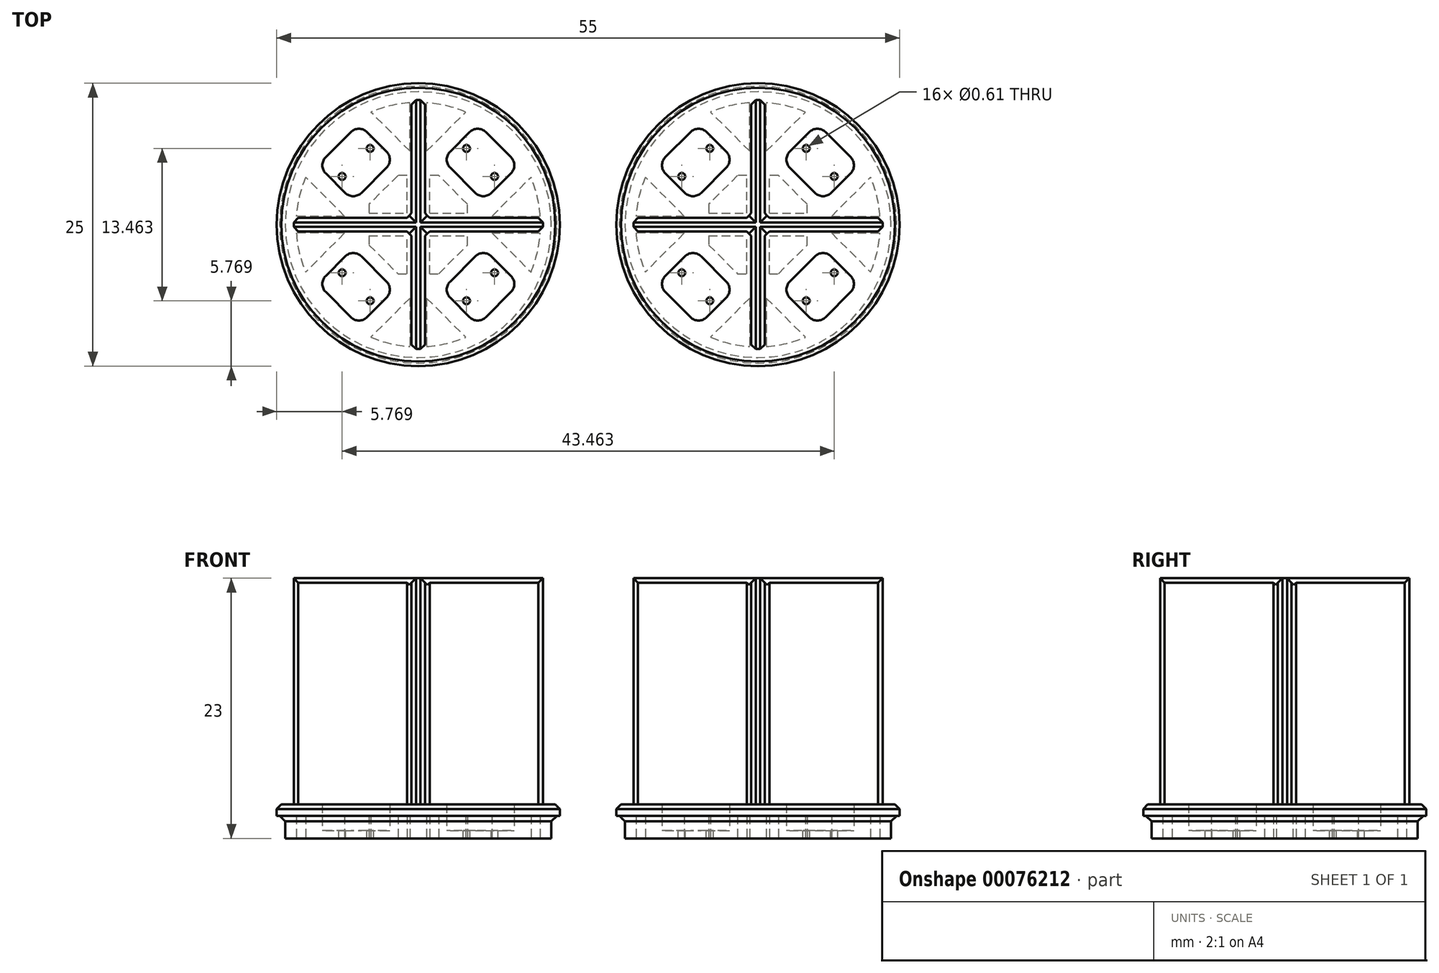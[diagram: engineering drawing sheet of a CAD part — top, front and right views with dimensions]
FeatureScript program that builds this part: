
annotation { "Feature Type Name" : "Feature", "Feature Type Description" : "" }
export const myFeature = defineFeature(function(context is Context, id is Id, definition is map)
    precondition{}
    {
        {
            var Q0;
            Q0=qCreatedBy(makeId("Top.planeOp"),FACE);
            var sketch = newSketch(context, id + "F0", { "sketchPlane" : qUnion([Q0])});
            skCircle(sketch, "E0", {"center": v(0, 0) * mm, "radius": 12.5 * mm});
            skSolve(sketch);
        }
        {
            var Q0;
            Q0=makeQuery(id+"F0.imprint","IMPRINT",FACE,{"disambiguationData":[TD([[makeQuery(id+"F0.imprint","IMPRINT",EDGE,{"derivedFrom":sQuery(id+"F0.wireOp",EDGE,"E0")}),1.0]])]});
            extrude(context, id + "F1", {"entities" : qUnion([Q0]), "depth" : 3 * mm});
        }
        {
            var Q0;
            Q0=makeQuery(id+"F1.opExtrude","CAP_FACE",FACE,{"disambiguationData":[OSD([sQuery(id+"F0.wireOp",EDGE,"E0")])],"isStart":false});
            var sketch = newSketch(context, id + "F2", { "sketchPlane" : qUnion([Q0])});
            skLineSegment(sketch, "E1", {"start": v(0, 0) * mm, "end": v(12.5, 0) * mm});
            skLineSegment(sketch, "E2", {"start": v(0, 0) * mm, "end": v(0, 12.5) * mm});
            skLineSegment(sketch, "E3.0", {"start": v(5.25, 8.89) * mm, "end": v(8.89, 5.25) * mm});
            skLineSegment(sketch, "E3.1", {"start": v(8.89, 5.25) * mm, "end": v(5.74, 2.1) * mm});
            skLineSegment(sketch, "E3.2", {"start": v(5.74, 2.1) * mm, "end": v(2.1, 5.74) * mm});
            skLineSegment(sketch, "E3.3", {"start": v(2.1, 5.74) * mm, "end": v(5.25, 8.89) * mm});
            skPoint(sketch, "E4.center", {"position": v(0, 0) * mm});
            skLineSegment(sketch, "E5.1.0", {"start": v(5.74, -2.1) * mm, "end": v(8.89, -5.25) * mm});
            skLineSegment(sketch, "E5.1.1", {"start": v(8.89, -5.25) * mm, "end": v(5.25, -8.89) * mm});
            skLineSegment(sketch, "E5.1.2", {"start": v(2.1, -5.74) * mm, "end": v(5.74, -2.1) * mm});
            skLineSegment(sketch, "E5.1.3", {"start": v(5.25, -8.89) * mm, "end": v(2.1, -5.74) * mm});
            skLineSegment(sketch, "E5.2.0", {"start": v(-2.1, -5.74) * mm, "end": v(-5.25, -8.89) * mm});
            skLineSegment(sketch, "E5.2.1", {"start": v(-5.25, -8.89) * mm, "end": v(-8.89, -5.25) * mm});
            skLineSegment(sketch, "E5.2.2", {"start": v(-5.74, -2.1) * mm, "end": v(-2.1, -5.74) * mm});
            skLineSegment(sketch, "E5.2.3", {"start": v(-8.89, -5.25) * mm, "end": v(-5.74, -2.1) * mm});
            skLineSegment(sketch, "E5.3.0", {"start": v(-5.74, 2.1) * mm, "end": v(-8.89, 5.25) * mm});
            skLineSegment(sketch, "E5.3.1", {"start": v(-8.89, 5.25) * mm, "end": v(-5.25, 8.89) * mm});
            skLineSegment(sketch, "E5.3.2", {"start": v(-2.1, 5.74) * mm, "end": v(-5.74, 2.1) * mm});
            skLineSegment(sketch, "E5.3.3", {"start": v(-5.25, 8.89) * mm, "end": v(-2.1, 5.74) * mm});
            skLineSegment(sketch, "E5.anchor1", {"start": v(0, 0) * mm, "end": v(2.1, 5.74) * mm, "construction": true});
            skLineSegment(sketch, "E5.anchor2", {"start": v(0, 0) * mm, "end": v(-5.74, 2.1) * mm, "construction": true});
            skSolve(sketch);
        }
        {
            var Q0;
            Q0=makeQuery(id+"F2.imprint","IMPRINT",FACE,{"disambiguationData":[TD([[makeQuery(id+"F2.imprint","IMPRINT",EDGE,{"derivedFrom":sQuery(id+"F2.wireOp",EDGE,"E5.3.0")}),-1.0]])]});
            var Q1;
            Q1=makeQuery(id+"F2.imprint","IMPRINT",FACE,{"disambiguationData":[TD([[makeQuery(id+"F2.imprint","IMPRINT",EDGE,{"derivedFrom":sQuery(id+"F2.wireOp",EDGE,"E3.0")}),-1.0]])]});
            var Q2;
            Q2=makeQuery(id+"F2.imprint","IMPRINT",FACE,{"disambiguationData":[TD([[makeQuery(id+"F2.imprint","IMPRINT",EDGE,{"derivedFrom":sQuery(id+"F2.wireOp",EDGE,"E5.1.0")}),-1.0]])]});
            var Q3;
            Q3=makeQuery(id+"F2.imprint","IMPRINT",FACE,{"disambiguationData":[TD([[makeQuery(id+"F2.imprint","IMPRINT",EDGE,{"derivedFrom":sQuery(id+"F2.wireOp",EDGE,"E5.2.0")}),-1.0]])]});
            extrude(context, id + "F3", {"entities" : qUnion([Q0, Q1, Q2, Q3]), "operationType" : NewBodyOperationType.REMOVE, "oppositeDirection" : true, "depth" : 2.3 * mm});
        }
        {
            var Q0;
            Q0=makeQuery(id+"F3.boolean.opBoolean","COPY",FACE,{"derivedFrom":makeQuery(id+"F3.opExtrude","CAP_FACE",FACE,{"disambiguationData":[OSD([sQuery(id+"F2.wireOp",EDGE,"E3.0"),sQuery(id+"F2.wireOp",EDGE,"E3.1"),sQuery(id+"F2.wireOp",EDGE,"E3.2"),sQuery(id+"F2.wireOp",EDGE,"E3.3")])],"isStart":false})});
            var sketch = newSketch(context, id + "F4", { "sketchPlane" : qUnion([Q0])});
            skCircle(sketch, "E6", {"center": v(4.26, 6.73) * mm, "radius": 0.3 * mm});
            skCircle(sketch, "E7", {"center": v(6.73, 4.26) * mm, "radius": 0.3 * mm});
            skPoint(sketch, "E8.orphan", {"position": v(5.83, 8.3) * mm});
            skPoint(sketch, "E9.orphan", {"position": v(2.68, 5.16) * mm});
            skPoint(sketch, "E10.orphan", {"position": v(3.67, 7.31) * mm});
            skPoint(sketch, "E11.orphan", {"position": v(7.07, 7.07) * mm});
            skPoint(sketch, "E12.start.orphan", {"position": v(3.92, 3.92) * mm});
            skPoint(sketch, "E13.orphan", {"position": v(5.16, 2.68) * mm});
            skPoint(sketch, "E14.orphan", {"position": v(8.3, 5.83) * mm});
            skPoint(sketch, "E15.orphan", {"position": v(7.31, 3.67) * mm});
            skCircle(sketch, "E16.1.0", {"center": v(6.73, -4.26) * mm, "radius": 0.3 * mm});
            skCircle(sketch, "E16.1.1", {"center": v(4.26, -6.73) * mm, "radius": 0.3 * mm});
            skCircle(sketch, "E16.2.0", {"center": v(-4.26, -6.73) * mm, "radius": 0.3 * mm});
            skCircle(sketch, "E16.2.1", {"center": v(-6.73, -4.26) * mm, "radius": 0.3 * mm});
            skCircle(sketch, "E16.3.0", {"center": v(-6.73, 4.26) * mm, "radius": 0.3 * mm});
            skCircle(sketch, "E16.3.1", {"center": v(-4.26, 6.73) * mm, "radius": 0.3 * mm});
            skPoint(sketch, "E16.center", {"position": v(0, 0) * mm});
            skLineSegment(sketch, "E16.anchor1", {"start": v(0, 0) * mm, "end": v(4.26, 6.73) * mm, "construction": true});
            skLineSegment(sketch, "E16.anchor2", {"start": v(0, 0) * mm, "end": v(-6.73, 4.26) * mm, "construction": true});
            skSolve(sketch);
        }
        {
            var Q0;
            Q0=makeQuery(id+"F4.imprint","IMPRINT",FACE,{"disambiguationData":[TD([[makeQuery(id+"F4.imprint","IMPRINT",EDGE,{"derivedFrom":sQuery(id+"F4.wireOp",EDGE,"E16.3.1")}),1.0]])]});
            var Q1;
            Q1=makeQuery(id+"F4.imprint","IMPRINT",FACE,{"disambiguationData":[TD([[makeQuery(id+"F4.imprint","IMPRINT",EDGE,{"derivedFrom":sQuery(id+"F4.wireOp",EDGE,"E16.3.0")}),1.0]])]});
            var Q2;
            Q2=makeQuery(id+"F4.imprint","IMPRINT",FACE,{"disambiguationData":[TD([[makeQuery(id+"F4.imprint","IMPRINT",EDGE,{"derivedFrom":sQuery(id+"F4.wireOp",EDGE,"E6")}),1.0]])]});
            var Q3;
            Q3=makeQuery(id+"F4.imprint","IMPRINT",FACE,{"disambiguationData":[TD([[makeQuery(id+"F4.imprint","IMPRINT",EDGE,{"derivedFrom":sQuery(id+"F4.wireOp",EDGE,"E7")}),1.0]])]});
            var Q4;
            Q4=makeQuery(id+"F4.imprint","IMPRINT",FACE,{"disambiguationData":[TD([[makeQuery(id+"F4.imprint","IMPRINT",EDGE,{"derivedFrom":sQuery(id+"F4.wireOp",EDGE,"E16.1.0")}),1.0]])]});
            var Q5;
            Q5=makeQuery(id+"F4.imprint","IMPRINT",FACE,{"disambiguationData":[TD([[makeQuery(id+"F4.imprint","IMPRINT",EDGE,{"derivedFrom":sQuery(id+"F4.wireOp",EDGE,"E16.1.1")}),1.0]])]});
            var Q6;
            Q6=makeQuery(id+"F4.imprint","IMPRINT",FACE,{"disambiguationData":[TD([[makeQuery(id+"F4.imprint","IMPRINT",EDGE,{"derivedFrom":sQuery(id+"F4.wireOp",EDGE,"E16.2.0")}),1.0]])]});
            var Q7;
            Q7=makeQuery(id+"F4.imprint","IMPRINT",FACE,{"disambiguationData":[TD([[makeQuery(id+"F4.imprint","IMPRINT",EDGE,{"derivedFrom":sQuery(id+"F4.wireOp",EDGE,"E16.2.1")}),1.0]])]});
            extrude(context, id + "F5", {"entities" : qUnion([Q0, Q1, Q2, Q3, Q4, Q5, Q6, Q7]), "operationType" : NewBodyOperationType.REMOVE, "endBound" : BoundingType.UP_TO_NEXT, "oppositeDirection" : true, "depth" : 25 * mm});
        }
        {
            var Q0;
            Q0=makeQuery(id+"F3.boolean.opBoolean","COPY",EDGE,{"derivedFrom":makeQuery(id+"F3.opExtrude","SWEPT_EDGE",EDGE,{"disambiguationData":[OSD([sQuery(id+"F2.wireOp",EDGE,"E3.0"),sQuery(id+"F2.wireOp",EDGE,"E3.3")])]})});
            var Q1;
            Q1=makeQuery(id+"F3.boolean.opBoolean","COPY",EDGE,{"derivedFrom":makeQuery(id+"F3.opExtrude","SWEPT_EDGE",EDGE,{"disambiguationData":[OSD([sQuery(id+"F2.wireOp",EDGE,"E5.3.1"),sQuery(id+"F2.wireOp",EDGE,"E5.3.3")])]})});
            var Q2;
            Q2=makeQuery(id+"F3.boolean.opBoolean","COPY",EDGE,{"derivedFrom":makeQuery(id+"F3.opExtrude","SWEPT_EDGE",EDGE,{"disambiguationData":[OSD([sQuery(id+"F2.wireOp",EDGE,"E5.2.2"),sQuery(id+"F2.wireOp",EDGE,"E5.2.3")])]})});
            var Q3;
            Q3=makeQuery(id+"F3.boolean.opBoolean","COPY",EDGE,{"derivedFrom":makeQuery(id+"F3.opExtrude","SWEPT_EDGE",EDGE,{"disambiguationData":[OSD([sQuery(id+"F2.wireOp",EDGE,"E5.1.0"),sQuery(id+"F2.wireOp",EDGE,"E5.1.2")])]})});
            var Q4;
            Q4=makeQuery(id+"F3.boolean.opBoolean","COPY",EDGE,{"derivedFrom":makeQuery(id+"F3.opExtrude","SWEPT_EDGE",EDGE,{"disambiguationData":[OSD([sQuery(id+"F2.wireOp",EDGE,"E3.2"),sQuery(id+"F2.wireOp",EDGE,"E3.3")])]})});
            var Q5;
            Q5=makeQuery(id+"F3.boolean.opBoolean","COPY",EDGE,{"derivedFrom":makeQuery(id+"F3.opExtrude","SWEPT_EDGE",EDGE,{"disambiguationData":[OSD([sQuery(id+"F2.wireOp",EDGE,"E5.3.0"),sQuery(id+"F2.wireOp",EDGE,"E5.3.1")])]})});
            var Q6;
            Q6=makeQuery(id+"F3.boolean.opBoolean","COPY",EDGE,{"derivedFrom":makeQuery(id+"F3.opExtrude","SWEPT_EDGE",EDGE,{"disambiguationData":[OSD([sQuery(id+"F2.wireOp",EDGE,"E5.2.1"),sQuery(id+"F2.wireOp",EDGE,"E5.2.3")])]})});
            var Q7;
            Q7=makeQuery(id+"F3.boolean.opBoolean","COPY",EDGE,{"derivedFrom":makeQuery(id+"F3.opExtrude","SWEPT_EDGE",EDGE,{"disambiguationData":[OSD([sQuery(id+"F2.wireOp",EDGE,"E5.1.2"),sQuery(id+"F2.wireOp",EDGE,"E5.1.3")])]})});
            var Q8;
            Q8=makeQuery(id+"F3.boolean.opBoolean","COPY",EDGE,{"derivedFrom":makeQuery(id+"F3.opExtrude","SWEPT_EDGE",EDGE,{"disambiguationData":[OSD([sQuery(id+"F2.wireOp",EDGE,"E5.3.2"),sQuery(id+"F2.wireOp",EDGE,"E5.3.3")])]})});
            var Q9;
            Q9=makeQuery(id+"F3.boolean.opBoolean","COPY",EDGE,{"derivedFrom":makeQuery(id+"F3.opExtrude","SWEPT_EDGE",EDGE,{"disambiguationData":[OSD([sQuery(id+"F2.wireOp",EDGE,"E3.0"),sQuery(id+"F2.wireOp",EDGE,"E3.1")])]})});
            var Q10;
            Q10=makeQuery(id+"F3.boolean.opBoolean","COPY",EDGE,{"derivedFrom":makeQuery(id+"F3.opExtrude","SWEPT_EDGE",EDGE,{"disambiguationData":[OSD([sQuery(id+"F2.wireOp",EDGE,"E5.1.0"),sQuery(id+"F2.wireOp",EDGE,"E5.1.1")])]})});
            var Q11;
            Q11=makeQuery(id+"F3.boolean.opBoolean","COPY",EDGE,{"derivedFrom":makeQuery(id+"F3.opExtrude","SWEPT_EDGE",EDGE,{"disambiguationData":[OSD([sQuery(id+"F2.wireOp",EDGE,"E5.2.0"),sQuery(id+"F2.wireOp",EDGE,"E5.2.2")])]})});
            var Q12;
            Q12=makeQuery(id+"F3.boolean.opBoolean","COPY",EDGE,{"derivedFrom":makeQuery(id+"F3.opExtrude","SWEPT_EDGE",EDGE,{"disambiguationData":[OSD([sQuery(id+"F2.wireOp",EDGE,"E5.3.0"),sQuery(id+"F2.wireOp",EDGE,"E5.3.2")])]})});
            var Q13;
            Q13=makeQuery(id+"F3.boolean.opBoolean","COPY",EDGE,{"derivedFrom":makeQuery(id+"F3.opExtrude","SWEPT_EDGE",EDGE,{"disambiguationData":[OSD([sQuery(id+"F2.wireOp",EDGE,"E5.2.0"),sQuery(id+"F2.wireOp",EDGE,"E5.2.1")])]})});
            var Q14;
            Q14=makeQuery(id+"F3.boolean.opBoolean","COPY",EDGE,{"derivedFrom":makeQuery(id+"F3.opExtrude","SWEPT_EDGE",EDGE,{"disambiguationData":[OSD([sQuery(id+"F2.wireOp",EDGE,"E5.1.1"),sQuery(id+"F2.wireOp",EDGE,"E5.1.3")])]})});
            var Q15;
            Q15=makeQuery(id+"F3.boolean.opBoolean","COPY",EDGE,{"derivedFrom":makeQuery(id+"F3.opExtrude","SWEPT_EDGE",EDGE,{"disambiguationData":[OSD([sQuery(id+"F2.wireOp",EDGE,"E3.1"),sQuery(id+"F2.wireOp",EDGE,"E3.2")])]})});
            fillet(context, id + "F6", {"entities" : qUnion([Q0, Q1, Q2, Q3, Q4, Q5, Q6, Q7, Q8, Q9, Q10, Q11, Q12, Q13, Q14, Q15]), "radius" : 1 * mm, "tangentPropagation" : true, "allowEdgeOverflow" : false});
        }
        {
            var Q0;
            Q0=makeQuery(id+"F1.opExtrude","CAP_FACE",FACE,{"disambiguationData":[OSD([sQuery(id+"F0.wireOp",EDGE,"E0")])],"isStart":true});
            var sketch = newSketch(context, id + "F7", { "sketchPlane" : qUnion([Q0])});
            skCircle(sketch, "E17.cCircle", {"center": v(0, 0) * mm, "radius": 4.34 * mm, "construction": true});
            skLineSegment(sketch, "E17.0", {"start": v(1.8, 4.34) * mm, "end": v(4.34, 1.8) * mm});
            skLineSegment(sketch, "E17.1", {"start": v(4.34, 1.8) * mm, "end": v(4.34, 1) * mm});
            skLineSegment(sketch, "E17.2", {"start": v(4.34, -1.8) * mm, "end": v(1.8, -4.34) * mm});
            skLineSegment(sketch, "E17.3", {"start": v(1.8, -4.34) * mm, "end": v(1, -4.34) * mm});
            skLineSegment(sketch, "E17.4", {"start": v(-1.8, -4.34) * mm, "end": v(-4.34, -1.8) * mm});
            skLineSegment(sketch, "E17.5", {"start": v(-4.34, -1.8) * mm, "end": v(-4.34, -1) * mm});
            skLineSegment(sketch, "E17.6", {"start": v(-4.34, 1.8) * mm, "end": v(-1.8, 4.34) * mm});
            skLineSegment(sketch, "E17.7", {"start": v(-1.8, 4.34) * mm, "end": v(-1, 4.34) * mm});
            skPoint(sketch, "E17.0.midPoint", {"position": v(3.07, 3.07) * mm});
            skLineSegment(sketch, "E18.0", {"start": v(1, 4.34) * mm, "end": v(1, 1) * mm});
            skLineSegment(sketch, "E19.MirrorCS", {"start": v(-1, 4.34) * mm, "end": v(-1, 1) * mm});
            skPoint(sketch, "E20.orphan", {"position": v(0, 4.34) * mm});
            skPoint(sketch, "E21.end.orphan", {"position": v(0, -4.34) * mm});
            skLineSegment(sketch, "E22.0", {"start": v(-4.34, -1) * mm, "end": v(-1, -1) * mm});
            skCircle(sketch, "E23.0", {"center": v(0, 0) * mm, "radius": 7.5 * mm});
            skLineSegment(sketch, "E24.MirrorCS", {"start": v(-4.34, 1) * mm, "end": v(-1, 1) * mm});
            skPoint(sketch, "E25.start.orphan", {"position": v(-4.34, 0) * mm});
            skPoint(sketch, "E26.trimOffspring.end.orphan", {"position": v(4.34, 0) * mm});
            skLineSegment(sketch, "E27.trimOffspring", {"start": v(1, -1) * mm, "end": v(1, -4.34) * mm});
            skLineSegment(sketch, "E28.trimOffspring", {"start": v(-1, -1) * mm, "end": v(-1, -4.34) * mm});
            skLineSegment(sketch, "E29.trimOffspring", {"start": v(1, 1) * mm, "end": v(4.34, 1) * mm});
            skLineSegment(sketch, "E30.trimOffspring", {"start": v(1, -1) * mm, "end": v(4.34, -1) * mm});
            skLineSegment(sketch, "E31.trimOffspring", {"start": v(-1, -4.34) * mm, "end": v(-1.8, -4.34) * mm});
            skLineSegment(sketch, "E32.trimOffspring", {"start": v(4.34, -1) * mm, "end": v(4.34, -1.8) * mm});
            skLineSegment(sketch, "E33.trimOffspring", {"start": v(-4.34, 1) * mm, "end": v(-4.34, 1.8) * mm});
            skLineSegment(sketch, "E34.trimOffspring", {"start": v(1, 4.34) * mm, "end": v(1.8, 4.34) * mm});
            skSolve(sketch);
        }
        {
            var Q0;
            Q0=makeQuery(id+"F7.imprint","IMPRINT",FACE,{"disambiguationData":[TD([[makeQuery(id+"F7.imprint","IMPRINT",EDGE,{"derivedFrom":sQuery(id+"F7.wireOp",EDGE,"E17.6")}),-1.0]])]});
            var Q1;
            Q1=makeQuery(id+"F7.imprint","IMPRINT",FACE,{"disambiguationData":[TD([[makeQuery(id+"F7.imprint","IMPRINT",EDGE,{"derivedFrom":sQuery(id+"F7.wireOp",EDGE,"E17.0")}),-1.0]])]});
            var Q2;
            Q2=makeQuery(id+"F7.imprint","IMPRINT",FACE,{"disambiguationData":[TD([[makeQuery(id+"F7.imprint","IMPRINT",EDGE,{"derivedFrom":sQuery(id+"F7.wireOp",EDGE,"E17.4")}),-1.0]])]});
            var Q3;
            Q3=makeQuery(id+"F7.imprint","IMPRINT",FACE,{"disambiguationData":[TD([[makeQuery(id+"F7.imprint","IMPRINT",EDGE,{"derivedFrom":sQuery(id+"F7.wireOp",EDGE,"E17.2")}),-1.0]])]});
            extrude(context, id + "F8", {"entities" : qUnion([Q0, Q1, Q2, Q3]), "operationType" : NewBodyOperationType.REMOVE, "oppositeDirection" : true, "depth" : 2 * mm});
        }
        {
            var Q0;
            Q0=makeQuery(id+"F1.opExtrude","CAP_FACE",FACE,{"disambiguationData":[OSD([sQuery(id+"F0.wireOp",EDGE,"E0")])],"isStart":true});
            var sketch = newSketch(context, id + "F9", { "sketchPlane" : qUnion([Q0])});
            skCircle(sketch, "E35", {"center": v(0, 0) * mm, "radius": 11.75 * mm});
            skSolve(sketch);
        }
        {
            var Q0;
            Q0=makeQuery(id+"F9.imprint","IMPRINT",FACE,{"disambiguationData":[TD([[makeQuery(id+"F9.imprint","IMPRINT",EDGE,{"derivedFrom":sQuery(id+"F9.wireOp",EDGE,"E35")}),-1.0]])]});
            extrude(context, id + "F10", {"entities" : qUnion([Q0]), "operationType" : NewBodyOperationType.REMOVE, "oppositeDirection" : true, "depth" : 2 * mm});
        }
        {
            var Q0;
            Q0=makeQuery(id+"F10.boolean.opBoolean","COPY",EDGE,{"derivedFrom":makeQuery(id+"F10.opExtrude","CAP_EDGE",EDGE,{"disambiguationData":[OSD([sQuery(id+"F9.wireOp",EDGE,"E35")])],"isStart":false})});
            chamfer(context, id + "F11", {"entities" : qUnion([Q0]), "width" : 0.5 * mm, "tangentPropagation" : true});
        }
        {
            var Q0;
            Q0=qCreatedBy(makeId("Top.planeOp"),FACE);
            var sketch = newSketch(context, id + "F12", { "sketchPlane" : qUnion([Q0])});
            skLineSegment(sketch, "E36", {"start": v(6.5, -0.74) * mm, "end": v(9.95, -4.19) * mm});
            skLineSegment(sketch, "E37", {"start": v(6.5, 0.74) * mm, "end": v(9.95, 4.19) * mm});
            skArc(sketch, "E38", {"start": v(9.95, -4.19) * mm, "mid": v(10.5, -2.5) * mm, "end": v(10.77, -0.74) * mm});
            skLineSegment(sketch, "E39.0", {"start": v(6.5, -0.74) * mm, "end": v(10.77, -0.74) * mm});
            skLineSegment(sketch, "E40.0", {"start": v(6.5, 0.74) * mm, "end": v(10.77, 0.74) * mm});
            skArc(sketch, "E41.trimOffspring", {"start": v(10.77, 0.74) * mm, "mid": v(10.5, 2.5) * mm, "end": v(9.95, 4.19) * mm});
            skLineSegment(sketch, "E42.1.0", {"start": v(-0.74, -6.5) * mm, "end": v(-4.19, -9.95) * mm});
            skArc(sketch, "E42.1.1", {"start": v(-4.19, -9.95) * mm, "mid": v(-2.5, -10.5) * mm, "end": v(-0.74, -10.77) * mm});
            skLineSegment(sketch, "E42.1.2", {"start": v(-0.74, -6.5) * mm, "end": v(-0.74, -10.77) * mm});
            skLineSegment(sketch, "E42.1.3", {"start": v(0.74, -6.5) * mm, "end": v(0.74, -10.77) * mm});
            skLineSegment(sketch, "E42.1.4", {"start": v(0.74, -6.5) * mm, "end": v(4.19, -9.95) * mm});
            skArc(sketch, "E42.1.5", {"start": v(0.74, -10.77) * mm, "mid": v(2.5, -10.5) * mm, "end": v(4.19, -9.95) * mm});
            skLineSegment(sketch, "E42.2.0", {"start": v(-6.5, 0.74) * mm, "end": v(-9.95, 4.19) * mm});
            skArc(sketch, "E42.2.1", {"start": v(-9.95, 4.19) * mm, "mid": v(-10.5, 2.5) * mm, "end": v(-10.77, 0.74) * mm});
            skLineSegment(sketch, "E42.2.2", {"start": v(-6.5, 0.74) * mm, "end": v(-10.77, 0.74) * mm});
            skLineSegment(sketch, "E42.2.3", {"start": v(-6.5, -0.74) * mm, "end": v(-10.77, -0.74) * mm});
            skLineSegment(sketch, "E42.2.4", {"start": v(-6.5, -0.74) * mm, "end": v(-9.95, -4.19) * mm});
            skArc(sketch, "E42.2.5", {"start": v(-10.77, -0.74) * mm, "mid": v(-10.5, -2.5) * mm, "end": v(-9.95, -4.19) * mm});
            skLineSegment(sketch, "E42.3.0", {"start": v(0.74, 6.5) * mm, "end": v(4.19, 9.95) * mm});
            skArc(sketch, "E42.3.1", {"start": v(4.19, 9.95) * mm, "mid": v(2.5, 10.5) * mm, "end": v(0.74, 10.77) * mm});
            skLineSegment(sketch, "E42.3.2", {"start": v(0.74, 6.5) * mm, "end": v(0.74, 10.77) * mm});
            skLineSegment(sketch, "E42.3.3", {"start": v(-0.74, 6.5) * mm, "end": v(-0.74, 10.77) * mm});
            skLineSegment(sketch, "E42.3.4", {"start": v(-0.74, 6.5) * mm, "end": v(-4.19, 9.95) * mm});
            skArc(sketch, "E42.3.5", {"start": v(-0.74, 10.77) * mm, "mid": v(-2.5, 10.5) * mm, "end": v(-4.19, 9.95) * mm});
            skLineSegment(sketch, "E42.anchor1", {"start": v(0, 0) * mm, "end": v(9.95, -4.19) * mm, "construction": true});
            skLineSegment(sketch, "E42.anchor2", {"start": v(0, 0) * mm, "end": v(4.19, 9.95) * mm, "construction": true});
            skSolve(sketch);
        }
        {
            var Q0;
            Q0=makeQuery(id+"F12.imprint","IMPRINT",FACE,{"disambiguationData":[TD([[makeQuery(id+"F12.imprint","IMPRINT",EDGE,{"derivedFrom":sQuery(id+"F12.wireOp",EDGE,"E42.1.0")}),1.0]])]});
            var Q1;
            Q1=makeQuery(id+"F12.imprint","IMPRINT",FACE,{"disambiguationData":[TD([[makeQuery(id+"F12.imprint","IMPRINT",EDGE,{"derivedFrom":sQuery(id+"F12.wireOp",EDGE,"E42.1.3")}),1.0]])]});
            var Q2;
            Q2=makeQuery(id+"F12.imprint","IMPRINT",FACE,{"disambiguationData":[TD([[makeQuery(id+"F12.imprint","IMPRINT",EDGE,{"derivedFrom":sQuery(id+"F12.wireOp",EDGE,"E36")}),1.0]])]});
            var Q3;
            Q3=makeQuery(id+"F12.imprint","IMPRINT",FACE,{"disambiguationData":[TD([[makeQuery(id+"F12.imprint","IMPRINT",EDGE,{"derivedFrom":sQuery(id+"F12.wireOp",EDGE,"E37")}),-1.0]])]});
            var Q4;
            Q4=makeQuery(id+"F12.imprint","IMPRINT",FACE,{"disambiguationData":[TD([[makeQuery(id+"F12.imprint","IMPRINT",EDGE,{"derivedFrom":sQuery(id+"F12.wireOp",EDGE,"E42.3.0")}),1.0]])]});
            var Q5;
            Q5=makeQuery(id+"F12.imprint","IMPRINT",FACE,{"disambiguationData":[TD([[makeQuery(id+"F12.imprint","IMPRINT",EDGE,{"derivedFrom":sQuery(id+"F12.wireOp",EDGE,"E42.3.3")}),1.0]])]});
            var Q6;
            Q6=makeQuery(id+"F12.imprint","IMPRINT",FACE,{"disambiguationData":[TD([[makeQuery(id+"F12.imprint","IMPRINT",EDGE,{"derivedFrom":sQuery(id+"F12.wireOp",EDGE,"E42.2.0")}),1.0]])]});
            var Q7;
            Q7=makeQuery(id+"F12.imprint","IMPRINT",FACE,{"disambiguationData":[TD([[makeQuery(id+"F12.imprint","IMPRINT",EDGE,{"derivedFrom":sQuery(id+"F12.wireOp",EDGE,"E42.2.3")}),1.0]])]});
            extrude(context, id + "F13", {"entities" : qUnion([Q0, Q1, Q2, Q3, Q4, Q5, Q6, Q7]), "operationType" : NewBodyOperationType.REMOVE, "depth" : 2 * mm});
        }
        {
            var Q0;
            Q0=makeQuery(id+"F1.opExtrude","CAP_FACE",FACE,{"disambiguationData":[OSD([sQuery(id+"F0.wireOp",EDGE,"E0")])],"isStart":false});
            var sketch = newSketch(context, id + "F14", { "sketchPlane" : qUnion([Q0])});
            skLineSegment(sketch, "E43.0", {"start": v(-11, -0.6) * mm, "end": v(-0.6, -0.6) * mm});
            skCircle(sketch, "E44.0", {"center": v(0, 0) * mm, "radius": 17.5 * mm});
            skLineSegment(sketch, "E45.0", {"start": v(-11, 0.6) * mm, "end": v(-0.6, 0.6) * mm});
            skLineSegment(sketch, "E46.0", {"start": v(0.6, -11) * mm, "end": v(0.6, -0.6) * mm});
            skLineSegment(sketch, "E47.0", {"start": v(-0.6, -11) * mm, "end": v(-0.6, -0.6) * mm});
            skPoint(sketch, "E48.orphan", {"position": v(11, 0) * mm});
            skPoint(sketch, "E49.orphan", {"position": v(0, 11) * mm});
            skPoint(sketch, "E50.orphan", {"position": v(-11, 0) * mm});
            skPoint(sketch, "E51.orphan", {"position": v(0, -11) * mm});
            skLineSegment(sketch, "E52.trimOffspring", {"start": v(-0.6, 0.6) * mm, "end": v(-0.6, 11) * mm});
            skLineSegment(sketch, "E53.trimOffspring", {"start": v(0.6, 0.6) * mm, "end": v(0.6, 11) * mm});
            skLineSegment(sketch, "E54.trimOffspring", {"start": v(0.6, 0.6) * mm, "end": v(11, 0.6) * mm});
            skLineSegment(sketch, "E55.trimOffspring", {"start": v(0.6, -0.6) * mm, "end": v(11, -0.6) * mm});
            skLineSegment(sketch, "E56", {"start": v(-0.6, -11) * mm, "end": v(0.6, -11) * mm});
            skLineSegment(sketch, "E57", {"start": v(11, 0.6) * mm, "end": v(11, -0.6) * mm});
            skLineSegment(sketch, "E58", {"start": v(-11, 0.6) * mm, "end": v(-11, -0.6) * mm});
            skLineSegment(sketch, "E59", {"start": v(-0.6, 11) * mm, "end": v(0.6, 11) * mm});
            skSolve(sketch);
        }
        {
            var Q0;
            Q0=makeQuery(id+"F14.imprint","IMPRINT",FACE,{"disambiguationData":[TD([[makeQuery(id+"F14.imprint","IMPRINT",EDGE,{"derivedFrom":sQuery(id+"F14.wireOp",EDGE,"E43.0")}),1.0]])]});
            extrude(context, id + "F15", {"entities" : qUnion([Q0]), "operationType" : NewBodyOperationType.ADD, "depth" : 20 * mm});
        }
        {
            var Q0;
            Q0=makeQuery(id+"F15.opExtrude","SWEPT_EDGE",EDGE,{"disambiguationData":[OSD([sQuery(id+"F14.wireOp",EDGE,"E47.0"),sQuery(id+"F14.wireOp",EDGE,"E56")])]});
            var Q1;
            Q1=makeQuery(id+"F15.opExtrude","SWEPT_EDGE",EDGE,{"disambiguationData":[OSD([sQuery(id+"F14.wireOp",EDGE,"E46.0"),sQuery(id+"F14.wireOp",EDGE,"E56")])]});
            var Q2;
            Q2=makeQuery(id+"F15.opExtrude","SWEPT_EDGE",EDGE,{"disambiguationData":[OSD([sQuery(id+"F14.wireOp",EDGE,"E55.trimOffspring"),sQuery(id+"F14.wireOp",EDGE,"E57")])]});
            var Q3;
            Q3=makeQuery(id+"F15.opExtrude","SWEPT_EDGE",EDGE,{"disambiguationData":[OSD([sQuery(id+"F14.wireOp",EDGE,"E54.trimOffspring"),sQuery(id+"F14.wireOp",EDGE,"E57")])]});
            var Q4;
            Q4=makeQuery(id+"F15.opExtrude","SWEPT_EDGE",EDGE,{"disambiguationData":[OSD([sQuery(id+"F14.wireOp",EDGE,"E53.trimOffspring"),sQuery(id+"F14.wireOp",EDGE,"E59")])]});
            var Q5;
            Q5=makeQuery(id+"F15.opExtrude","SWEPT_EDGE",EDGE,{"disambiguationData":[OSD([sQuery(id+"F14.wireOp",EDGE,"E52.trimOffspring"),sQuery(id+"F14.wireOp",EDGE,"E59")])]});
            var Q6;
            Q6=makeQuery(id+"F15.opExtrude","SWEPT_EDGE",EDGE,{"disambiguationData":[OSD([sQuery(id+"F14.wireOp",EDGE,"E45.0"),sQuery(id+"F14.wireOp",EDGE,"E58")])]});
            var Q7;
            Q7=makeQuery(id+"F15.opExtrude","SWEPT_EDGE",EDGE,{"disambiguationData":[OSD([sQuery(id+"F14.wireOp",EDGE,"E43.0"),sQuery(id+"F14.wireOp",EDGE,"E58")])]});
            var Q8;
            Q8=makeQuery(id+"F15.opExtrude","CAP_EDGE",EDGE,{"disambiguationData":[OSD([sQuery(id+"F14.wireOp",EDGE,"E54.trimOffspring")])],"isStart":false});
            var Q9;
            Q9=makeQuery(id+"F15.opExtrude","CAP_EDGE",EDGE,{"disambiguationData":[OSD([sQuery(id+"F14.wireOp",EDGE,"E55.trimOffspring")])],"isStart":false});
            var Q10;
            Q10=makeQuery(id+"F15.opExtrude","CAP_EDGE",EDGE,{"disambiguationData":[OSD([sQuery(id+"F14.wireOp",EDGE,"E53.trimOffspring")])],"isStart":false});
            var Q11;
            Q11=makeQuery(id+"F15.opExtrude","CAP_EDGE",EDGE,{"disambiguationData":[OSD([sQuery(id+"F14.wireOp",EDGE,"E52.trimOffspring")])],"isStart":false});
            var Q12;
            Q12=makeQuery(id+"F15.opExtrude","CAP_EDGE",EDGE,{"disambiguationData":[OSD([sQuery(id+"F14.wireOp",EDGE,"E45.0")])],"isStart":false});
            var Q13;
            Q13=makeQuery(id+"F15.opExtrude","CAP_EDGE",EDGE,{"disambiguationData":[OSD([sQuery(id+"F14.wireOp",EDGE,"E43.0")])],"isStart":false});
            var Q14;
            Q14=makeQuery(id+"F15.opExtrude","CAP_EDGE",EDGE,{"disambiguationData":[OSD([sQuery(id+"F14.wireOp",EDGE,"E47.0")])],"isStart":false});
            var Q15;
            Q15=makeQuery(id+"F15.opExtrude","CAP_EDGE",EDGE,{"disambiguationData":[OSD([sQuery(id+"F14.wireOp",EDGE,"E46.0")])],"isStart":false});
            chamfer(context, id + "F16", {"entities" : qUnion([Q0, Q1, Q2, Q3, Q4, Q5, Q6, Q7, Q8, Q9, Q10, Q11, Q12, Q13, Q14, Q15]), "width" : 0.4 * mm, "tangentPropagation" : true});
        }
        {
            var Q0;
            Q0=makeQuery(id+"F15.opExtrude","SWEPT_EDGE",EDGE,{"disambiguationData":[OSD([sQuery(id+"F14.wireOp",EDGE,"E53.trimOffspring"),sQuery(id+"F14.wireOp",EDGE,"E54.trimOffspring")])]});
            var Q1;
            Q1=makeQuery(id+"F15.opExtrude","SWEPT_EDGE",EDGE,{"disambiguationData":[OSD([sQuery(id+"F14.wireOp",EDGE,"E46.0"),sQuery(id+"F14.wireOp",EDGE,"E55.trimOffspring")])]});
            var Q2;
            Q2=makeQuery(id+"F15.opExtrude","SWEPT_EDGE",EDGE,{"disambiguationData":[OSD([sQuery(id+"F14.wireOp",EDGE,"E43.0"),sQuery(id+"F14.wireOp",EDGE,"E47.0")])]});
            var Q3;
            Q3=makeQuery(id+"F15.opExtrude","SWEPT_EDGE",EDGE,{"disambiguationData":[OSD([sQuery(id+"F14.wireOp",EDGE,"E45.0"),sQuery(id+"F14.wireOp",EDGE,"E52.trimOffspring")])]});
            var Q4;
            Q4=makeQuery(id+"F15.opExtrude","CAP_EDGE",EDGE,{"disambiguationData":[OSD([sQuery(id+"F14.wireOp",EDGE,"E52.trimOffspring")])],"isStart":true});
            var Q5;
            Q5=makeQuery(id+"F15.opExtrude","CAP_EDGE",EDGE,{"disambiguationData":[OSD([sQuery(id+"F14.wireOp",EDGE,"E45.0")])],"isStart":true});
            var Q6;
            Q6=makeQuery(id+"F15.opExtrude","CAP_EDGE",EDGE,{"disambiguationData":[OSD([sQuery(id+"F14.wireOp",EDGE,"E54.trimOffspring")])],"isStart":true});
            var Q7;
            Q7=makeQuery(id+"F15.opExtrude","CAP_EDGE",EDGE,{"disambiguationData":[OSD([sQuery(id+"F14.wireOp",EDGE,"E53.trimOffspring")])],"isStart":true});
            var Q8;
            Q8=makeQuery(id+"F15.opExtrude","CAP_EDGE",EDGE,{"disambiguationData":[OSD([sQuery(id+"F14.wireOp",EDGE,"E55.trimOffspring")])],"isStart":true});
            var Q9;
            Q9=makeQuery(id+"F15.opExtrude","CAP_EDGE",EDGE,{"disambiguationData":[OSD([sQuery(id+"F14.wireOp",EDGE,"E46.0")])],"isStart":true});
            var Q10;
            Q10=makeQuery(id+"F15.opExtrude","CAP_EDGE",EDGE,{"disambiguationData":[OSD([sQuery(id+"F14.wireOp",EDGE,"E47.0")])],"isStart":true});
            var Q11;
            Q11=makeQuery(id+"F15.opExtrude","CAP_EDGE",EDGE,{"disambiguationData":[OSD([sQuery(id+"F14.wireOp",EDGE,"E43.0")])],"isStart":true});
            var Q12;
            Q12=makeQuery(id+"F1.opExtrude","CAP_EDGE",EDGE,{"disambiguationData":[OSD([sQuery(id+"F0.wireOp",EDGE,"E0")])],"isStart":false});
            chamfer(context, id + "F17", {"entities" : qUnion([Q0, Q1, Q2, Q3, Q4, Q5, Q6, Q7, Q8, Q9, Q10, Q11, Q12]), "width" : 0.4 * mm, "tangentPropagation" : true});
        }
        {
            var Q0;
            Q0=makeQuery(id+"F1.opExtrude","SWEPT_BODY",BODY,{"disambiguationData":[OSD([sQuery(id+"F0.wireOp",EDGE,"E0")])]});
            transform(context, id + "F18", {"entities" : qUnion([Q0]), "transformType" : TransformType.TRANSLATION_3D, "dx" : 30 * mm, "dy" : 0 * mm, "dz" : 0 * mm, "makeCopy" : true});
        }
    });
